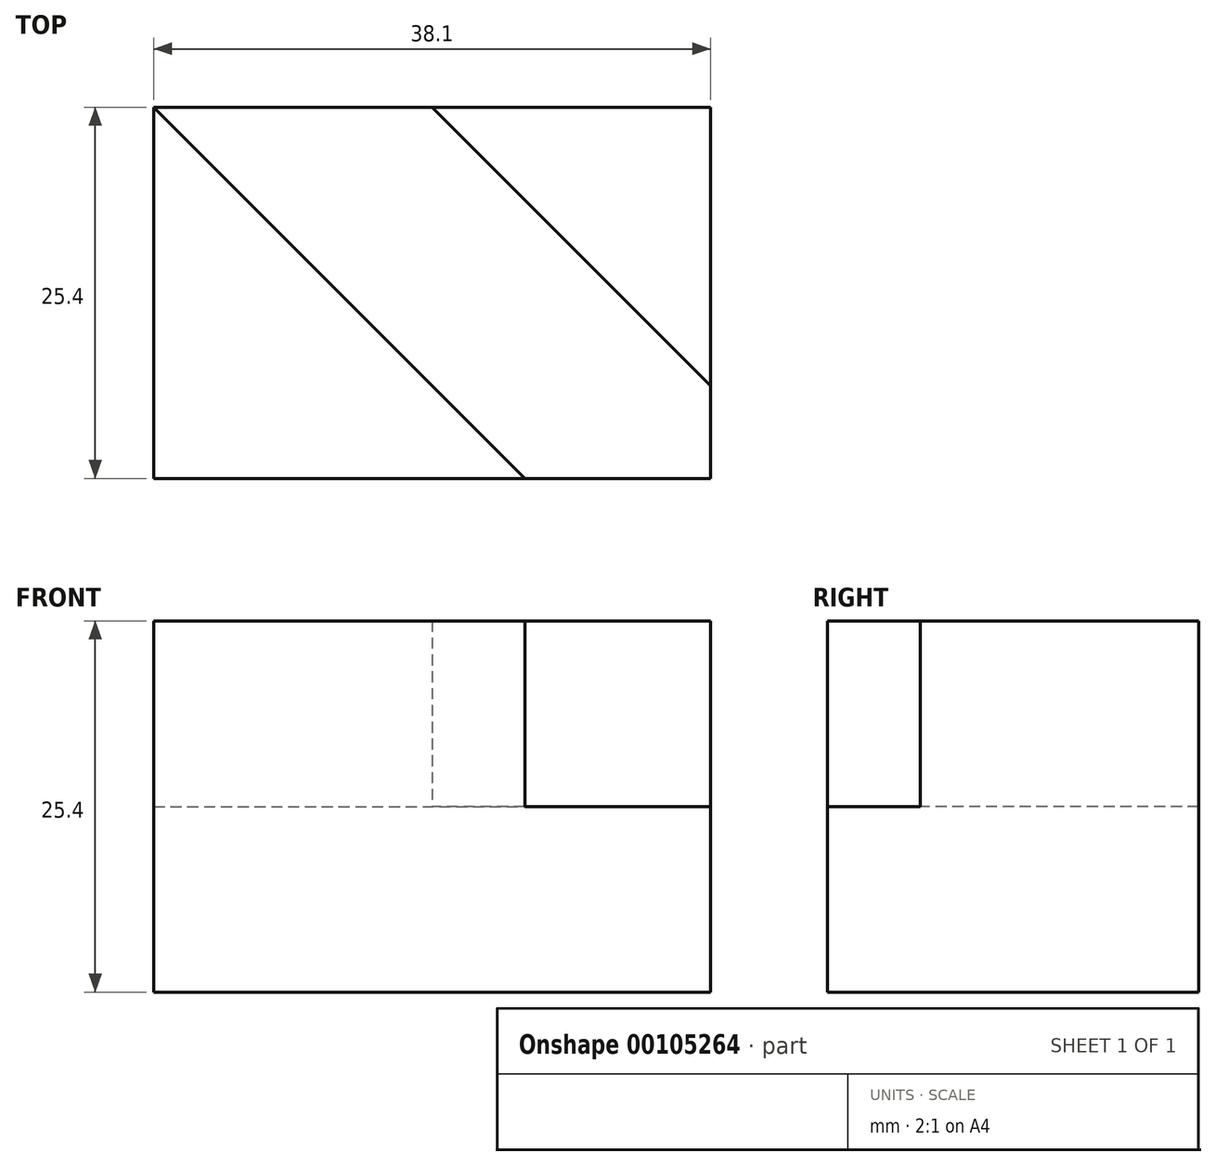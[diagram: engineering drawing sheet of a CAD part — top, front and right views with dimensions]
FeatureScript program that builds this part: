
annotation { "Feature Type Name" : "Feature", "Feature Type Description" : "" }
export const myFeature = defineFeature(function(context is Context, id is Id, definition is map)
    precondition{}
    {
        {
            var Q0;
            Q0=qCreatedBy(makeId("Top.planeOp"),FACE);
            var sketch = newSketch(context, id + "F0", { "sketchPlane" : qUnion([Q0])});
            skLineSegment(sketch, "E0.bottom", {"start": v(0, 0) * mm, "end": v(38.1, 0) * mm});
            skLineSegment(sketch, "E0.top", {"start": v(0, 25.4) * mm, "end": v(38.1, 25.4) * mm});
            skLineSegment(sketch, "E0.left", {"start": v(0, 0) * mm, "end": v(0, 25.4) * mm});
            skLineSegment(sketch, "E0.right", {"start": v(38.1, 0) * mm, "end": v(38.1, 25.4) * mm});
            skLineSegment(sketch, "E1", {"start": v(0, 25.4) * mm, "end": v(25.4, 0) * mm});
            skLineSegment(sketch, "E2", {"start": v(38.1, 6.35) * mm, "end": v(19.05, 25.4) * mm});
            skSolve(sketch);
        }
        {
            var Q0;
            {var subQ0=sQuery(id+"F0.wireOp",EDGE,"E1");Q0=makeQuery(id+"F0.imprint","IMPRINT",FACE,{"disambiguationData":[TD([[makeQuery(id+"F0.imprint","IMPRINT",EDGE,{"derivedFrom":subQ0}),1.0]])]});}
            extrude(context, id + "F1", {"entities" : qUnion([Q0]), "depth" : 12.7 * mm});
        }
        {
            var Q0;
            {var subQ0=sQuery(id+"F0.wireOp",EDGE,"E0.left");Q0=makeQuery(id+"F0.imprint","IMPRINT",FACE,{"disambiguationData":[TD([[makeQuery(id+"F0.imprint","IMPRINT",EDGE,{"derivedFrom":subQ0}),-1.0]])]});}
            var Q1;
            {var subQ3=sQuery(id+"F0.wireOp",EDGE,"E2");Q1=makeQuery(id+"F0.imprint","IMPRINT",FACE,{"disambiguationData":[TD([[makeQuery(id+"F0.imprint","IMPRINT",EDGE,{"derivedFrom":subQ3}),-1.0]])]});}
            extrude(context, id + "F2", {"entities" : qUnion([Q0, Q1]), "operationType" : NewBodyOperationType.ADD, "depth" : 25.4 * mm});
        }
    });
